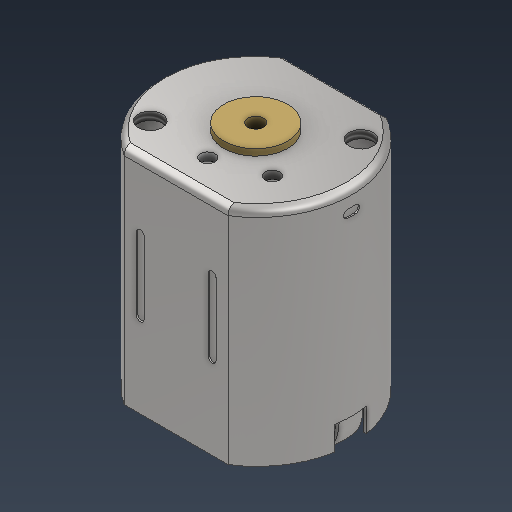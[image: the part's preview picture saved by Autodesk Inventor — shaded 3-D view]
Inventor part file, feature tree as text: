
AUTODESK INVENTOR PART (.ipt)
format: ipt  version: 2021 (Build 250183000, 183)  size: 619,008 bytes
history: native  units: mm
features: other x22, sketch x16, extrude x14, thread x2, fillet x2, loft x1
ambient origin geometry x8: Origin, YZ Plane, XZ Plane, XY Plane, X Axis, Y Axis, Z Axis, Center Point
bodies: Body1 (feature_tree)
feature tree (57):
  other  "Carcaça"
  other  "Sólido1"
  extrude  "Extrusão1"  Depth=5.920455mm
  extrude  "Extrusão18"  Depth=5.920455mm
  sketch  "Esboço21"  dims[d76=5.0mm d77=0.2mm]
  extrude  "Extrusão19"  Depth=0.2mm
  extrude  "Extrusão20"  Depth=0.1mm TaperAngle=0.0deg
  other  "Plano de trabalho7"
  extrude  "Extrusão21"  Depth=1.5mm
  other  "Plano de trabalho8"
  extrude  "Extrusão22"  Depth=1.5mm TaperAngle=0.0deg
  other  "Plano de trabalho9"
  extrude  "Extrusão23"  Depth=0.1mm TaperAngle=0.0deg
  other  "Plano de trabalho10"
  extrude  "Extrusão24"  Depth=1.5mm
  other  "Plano de trabalho11"
  other  "Vergar peça1"
  other  "Plano de trabalho12"
  other  "Vergar peça2"
  other  "Plano de trabalho13"
  other  "Plano de trabalho14"
  sketch  "Esboço30"  dims[d108=0.45mm d109=0.0mm d110=0.95mm d111=0.0mm d112=2.5mm d113=90.0deg d114=2.5mm d115=90.0deg]
  loft  "Transição2"
  sketch  "Esboço31"  dims[d116=0.5mm d117=-0.5mm]
  extrude  "Extrusão25"  Depth=0.45mm TaperAngle=0.0deg
  thread  "Rosca3"  [1 undecoded]
  thread  "Rosca4"  [1 undecoded]
  extrude  "Extrusão26"  [1 undecoded]
  extrude  "Extrusão27"  TaperAngle=0.0deg  [1 undecoded]
  extrude  "Extrusão28"  Depth=10.0mm TaperAngle=0.0deg
  fillet  "Arredondamento8"  Radius=0.5mm
  sketch  "Esboço37"  dims[d129=0.5mm d130=0.0mm d131=0.4mm d132=0.0mm]
  extrude  "Extrusão29"  Depth=0.5mm TaperAngle=0.0deg
  extrude  "Extrusão30"  Depth=0.15mm TaperAngle=0.0deg
  fillet  "Arredondamento9"  Radius=0.15mm
  sketch  "Esboço1"  dims[d11=13.5mm d12=0.0mm d73=5.920455mm]
  sketch  "Esboço20"  dims[d74=5.0mm d75=5.920455mm]
  other  "Contorno projetado8"
  sketch  "Esboço22"  dims[d87=5.0mm d88=0.5mm d89=5.0mm d90=0.1mm d91=0.0mm]
  sketch  "Esboço23"  dims[d92=0.1mm d93=0.0mm d94=1.5mm]
  other  "Contorno projetado9"
  sketch  "Esboço24"  dims[d95=1.5mm d96=0.2mm d97=0.0mm]
  sketch  "Esboço25"  dims[d98=0.5mm d99=1.0mm d100=0.25mm d101=0.1mm d102=0.0mm]
  other  "Contorno projetado10"
  sketch  "Esboço26"  dims[d103=0.1mm d104=0.0mm d105=1.5mm]
  sketch  "Esboço27"  dims[d106=2.0mm d107=1.5mm]
  other  "Contorno projetado11"
  other  "Arestas2"
  sketch  "Esboço32"  dims[d118=15.0mm d119=90.0deg d120=0.0mm d121=90.0deg]
  other  "Contorno projetado12"
  other  "Contorno projetado13"
  sketch  "Esboço33"  dims[d122=1.5mm d123=1.5mm d124=4.0mm d125=10.0mm d126=0.0mm d127=0.5mm d128=0.0mm]
  other  "Contorno projetado14"
  other  "Contorno projetado15"
  sketch  "Esboço38"  dims[d133=1.0mm d134=0.15mm d135=0.0mm d136=0.15mm d137=0.0mm]
  sketch  "Esboço39"  dims[d139=0.283339mm d140=0.2mm d141=0.2mm d142=0.2mm d143=12.0mm d144=6.0mm d145=6.0mm d146=3.0mm d147=0.15mm d148=0.0mm d149=3.0mm d151=60.0mm d153=360.0deg d155=0.3mm d156=0.0mm d157=0.1mm d158=0.9mm d27=0.5mm d28=0.872665mm d29=0.5mm d30=0.872665mm d31=0.5mm d32=0.872665mm d38=0.5mm d39=0.872665mm d40=0.5mm d41=0.872665mm]
  other  "Contorno projetado23"
note: 4 required parameter values undecoded (feature->parameter linkage not recoverable at this tier; creation-order binding heuristic only, values carry confidence <= 0.55)
